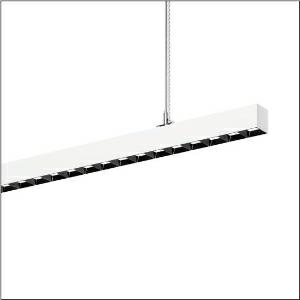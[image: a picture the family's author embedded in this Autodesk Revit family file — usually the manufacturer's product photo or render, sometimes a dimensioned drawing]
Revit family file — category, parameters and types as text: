
# Revit family: silica_21_51mx31dc4dwb
name_source: partatom
category: Lighting Fixtures
units: mm (PartAtom-declared; Revit-internal decimal feet)

## family parameters
Cut with Voids When Loaded = No
Host = Face
Light Source = No
Part Type = Normal
Room Calculation Point = No
Round Connector Dimension = Use Diameter
Shared = No

## types (1)
- --- (1 x LED, 18230 lm, 105.9 W, 4000K)
    Apparent Load = 106 VA
    CIE Flux Codes = 87 99 100 59 100
    Color Rendering = 80
    Color Temperature = 4000K
    Default Elevation = 1800 mm
    Description = Silica 21, office luminaire, primary light control with darklight reflector, of PMMA, black, CAT 2 (L<= 3000cd/m²), light emission: direct/indirect distribution, primary light characteristic: symmetric, installation type: suspended mounting, LED, rated luminous flux: 18.230lm, luminous efficacy: 172lm/W, light colour: 840, colour temperature: 4000K, control gear: DALI 2, with terminal, 3+2-pole, max. 2.5mm², mains connection: 220..240V, AC, 50/60Hz, rated input power: 105.9W, luminaire housing, of aluminium, traffic white (RAL 9016), length: 3.004mm, width: 53mm, height: 53mm, protection rating (complete): IP20, insulation class (complete): insulation class I (protective earthing), certification: CE, permissible operating ambient temperature: 0..+35°C, standard: EN 50419, packaging unit: 1 piece
    Height = 53 mm
    Lamp = 1 x LED
    Lamp Light Flux = 18230 lm
    Lamp Power = 105.9 W
    Lamp count = 1
    Length = 3004 mm
    Luminous efficacy = 172 lm/W
    Manufacturer = Siteco
    ModVariant = No
    Model = 51MX31DC4DWB
    Mounting Place = Ceiling
    Mounting Type = Pendant
    Number of Poles = 1
    OnlyDefault = Yes
    Power Factor = 1
    Product Name = Silica 21
    Product group = office luminaire | ceiling pendant
    ProductGroupID = 903
    Protection Class = Protection class I
    Protection Degree = IP 20
    RLX_Detail_Level = 1
    RLX_Emergency_Light_Flux = 0 lm
    RLX_Emergency_Type = 0
    RLX_Emergency_Type_DB = No
    RlxData = <blob elided: 64369 chars, md5=364a1b92>
    Socket = socket
    Standby Power = 0 W
    System Light Flux = 18230 lm
    System Power = 106 W
    Type Comments = factory setting: luminous flux: 100 % | dim-lin: 254 | 367 mA
    Type Image = l_1335871.jpg
    URL = http://relux.com
    VarID = @adj_121395
    Voltage = 0 V
    Weight = 0.00 kg
    Width = 53 mm

## geometry (parser evidence)
native form markers: Blend x4, Sweep x12
no freeform markers — native parametric forms only
